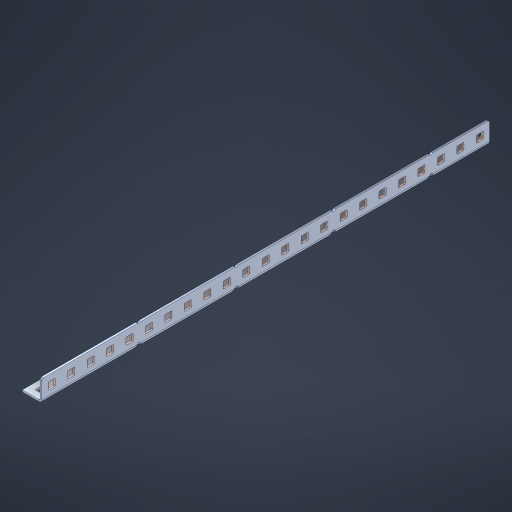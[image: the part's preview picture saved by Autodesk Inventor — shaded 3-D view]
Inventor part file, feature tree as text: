
AUTODESK INVENTOR PART (.ipt)
format: ipt  version: 2023 (Build 270158000, 158)  size: 807,936 bytes
history: native  units: in
note: dims shown in document units (in); Inventor stores cm internally (conversion verified against a paired STEP export)
features: other x51, extrude x45, sheet_metal_op x10, sketch x8, mirror x1, pattern_linear x1, chamfer x1
ambient origin geometry x8: Origin, YZ Plane, XZ Plane, XY Plane, X Axis, Y Axis, Z Axis, Center Point
bodies: Solid1 (feature_tree), Body (feature_tree)
feature tree (117):
  other  "Flange Pattern Plane"
  sheet_metal_op  "Flange Pattern"
  sheet_metal_op  "Body Pattern"
  other  "Arc Length"
  mirror  "Notch Mirror"
  pattern_linear  "Notch Pattern"  Spacing1=0.1875in  [1 undecoded]
  chamfer  "End Chamfer"
  extrude  "Half Cut"  Depth=0.0469in
  sketch  "Sketch1"  dims[d0=2.5in]
  other  "Plate1"
  sketch  "Sketch2"  dims[d1=11.5in]
  other  "Plate2"
  sheet_metal_op  "Bend1"
  sheet_metal_op  "Corner1"
  sketch  "Sketch3"  dims[d2=0.0469in]
  other  "Flange Pattern Sketch"
  sketch  "Sketch7"  dims[d3=0.0469in]
  other  "Srf1"
  other  "Srf2"
  sketch  "Sketch8"  dims[d4=0.0234in]
  sketch  "Sketch9"  dims[d5=0.0938in]
  other  "Srf91"
  sheet_metal_op  "Body Pattern Sketch"
  other  "Srf92"
  sketch  "Sketch13"  dims[d6=0.0469in]
  sketch  "Sketch14"  dims[d7=0.5in d8=90.0deg d9=0.0312in d10=0.1875in d11=0.0469in d12=0.0469in d16=0.182in d17=0.02in d18=0.0469in d19=0.0in d20=0.25in d21=0.25in d46=0.172in d47=1.0in d48=0.0in d49=0.182in d50=0.02in d51=0.25in d52=0.25in d53=0.0469in d54=0.0in d55=0.172in d56=1.0in d57=0.0in d60=9.0551in d62=0.5in d63=0.3937in d65=0.5in d85=0.1227in d86=0.1659in d88=0.04in d89=0.0469in d90=0.0in d91=0.04in d92=0.0491in d95=2.5in d96=0.04in d97=0.25in d98=45.0deg d101=0.0in d102=2.497in d131=0.5in d132=9.0551in d134=0.5in d139=0.5in]
  other  "Srf856"
  other  "Srf1310"
  other  "Srf1311"
  other  "Srf1312"
  other  "Srf1376"
  other  "Srf1377"
  other  "Srf1728"
  other  "Srf1755"
  other  "Srf1878"
  other  "Srf1879"
  other  "Srf1880"
  other  "Srf1881"
  other  "Srf1882"
  other  "Srf1883"
  other  "Srf1884"
  other  "Srf1885"
  other  "Srf1886"
  other  "Srf1887"
  other  "Srf1888"
  other  "Srf1889"
  other  "Srf1890"
  other  "Srf1891"
  other  "Srf1892"
  other  "Srf1893"
  other  "Srf1894"
  other  "Srf1942"
  other  "Srf1943"
  other  "Srf1944"
  other  "Srf1945"
  other  "Srf1946"
  other  "Srf1947"
  other  "Srf1948"
  other  "Srf1949"
  other  "Srf1950"
  other  "Srf1951"
  other  "Srf1952"
  other  "Srf1953"
  other  "Srf1954"
  other  "Srf1955"
  other  "Srf1956"
  other  "Srf1957"
  other  "Srf1958"
  sheet_metal_op  "Flange Stamp"
  sheet_metal_op  "Flange Circle"
  sheet_metal_op  "Body Stamp"
  sheet_metal_op  "Body Circle"
  sheet_metal_op  "Notch"
  extrude  "ExtrusionSrf2"  Depth=0.0469in
  extrude  "ExtrusionSrf92"  Depth=0.5in
  extrude  "ExtrusionSrf856"  Depth=0.02in
  extrude  "ExtrusionSrf1310"  Depth=0.0469in
  extrude  "ExtrusionSrf1311"  TaperAngle=0.0deg  [1 undecoded]
  extrude  "ExtrusionSrf1312"  Depth=0.5in
  extrude  "ExtrusionSrf1376"  Depth=0.5in
  extrude  "ExtrusionSrf1377"  Depth=0.5in
  extrude  "ExtrusionSrf1728"  Depth=0.5in TaperAngle=0.0deg
  extrude  "ExtrusionSrf1755"  Depth=0.5in
  extrude  "ExtrusionSrf1878"  Depth=0.02in
  extrude  "ExtrusionSrf1879"  Depth=0.5in
  extrude  "ExtrusionSrf1880"  Depth=0.5in
  extrude  "ExtrusionSrf1881"  Depth=0.0469in
  extrude  "ExtrusionSrf1882"  TaperAngle=0.0deg  [1 undecoded]
  extrude  "ExtrusionSrf1883"  Depth=0.5in
  extrude  "ExtrusionSrf1884"  Depth=0.5in TaperAngle=0.0deg
  extrude  "ExtrusionSrf1885"  Depth=0.5in
  extrude  "ExtrusionSrf1886"  Depth=0.5in
  extrude  "ExtrusionSrf1887"  Depth=0.5in
  extrude  "ExtrusionSrf1888"  Depth=0.5in
  extrude  "ExtrusionSrf1889"  Depth=0.5in
  extrude  "ExtrusionSrf1890"  Depth=0.0469in
  extrude  "ExtrusionSrf1891"  TaperAngle=0.0deg  [1 undecoded]
  extrude  "ExtrusionSrf1892"  Depth=0.5in
  extrude  "ExtrusionSrf1893"  Depth=0.5in
  extrude  "ExtrusionSrf1894"  Depth=0.5in
  extrude  "ExtrusionSrf1942"  Depth=0.5in TaperAngle=45.0deg
  extrude  "ExtrusionSrf1943"  TaperAngle=0.0deg  [1 undecoded]
  extrude  "ExtrusionSrf1944"  Depth=0.5in
  extrude  "ExtrusionSrf1945"  Depth=0.5in
  extrude  "ExtrusionSrf1946"  Depth=0.5in
  extrude  "ExtrusionSrf1947"  Depth=0.5in
  extrude  "ExtrusionSrf1948"  Depth=0.5in
  extrude  "ExtrusionSrf1949"  [1 undecoded]
  extrude  "ExtrusionSrf1950"  [1 undecoded]
  extrude  "ExtrusionSrf1951"  [1 undecoded]
  extrude  "ExtrusionSrf1952"  [1 undecoded]
  extrude  "ExtrusionSrf1953"  [1 undecoded]
  extrude  "ExtrusionSrf1954"  [1 undecoded]
  extrude  "ExtrusionSrf1955"  [1 undecoded]
  extrude  "ExtrusionSrf1956"  [1 undecoded]
  extrude  "ExtrusionSrf1957"  [1 undecoded]
  extrude  "ExtrusionSrf1958"  [1 undecoded]
note: 15 required parameter values undecoded (feature->parameter linkage not recoverable at this tier; creation-order binding heuristic only, values carry confidence <= 0.55)
